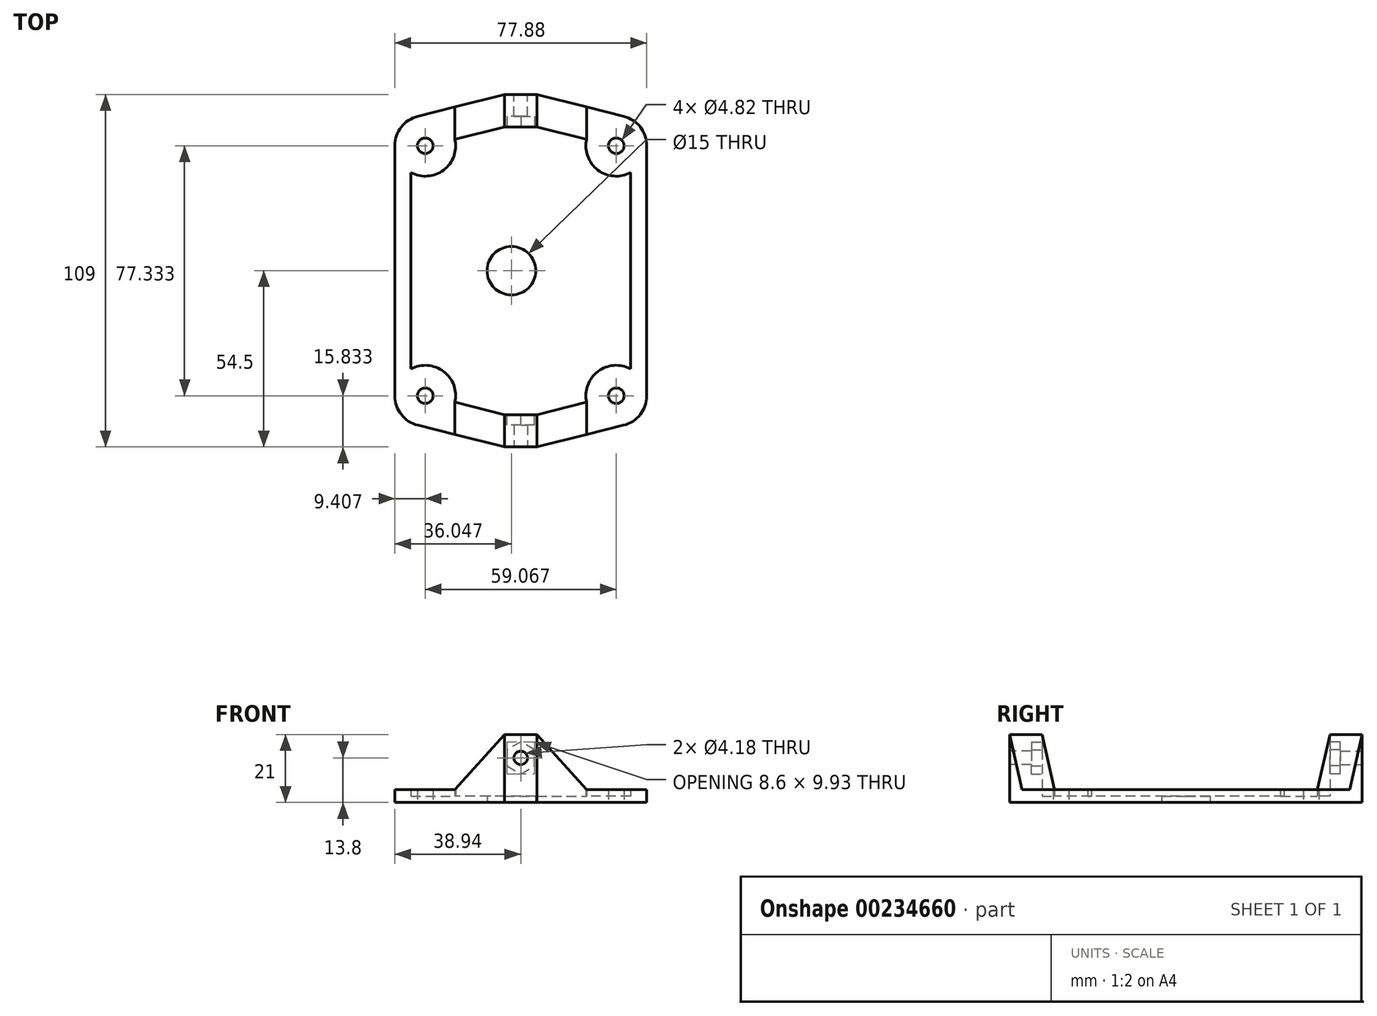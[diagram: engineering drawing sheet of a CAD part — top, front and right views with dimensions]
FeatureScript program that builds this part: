
annotation { "Feature Type Name" : "Feature", "Feature Type Description" : "" }
export const myFeature = defineFeature(function(context is Context, id is Id, definition is map)
    precondition{}
    {
        {
            var Q0;
            Q0=qCreatedBy(makeId("Top.planeOp"),FACE);
            var sketch = newSketch(context, id + "F0", { "sketchPlane" : qUnion([Q0])});
            skLineSegment(sketch, "E0.top", {"start": v(44.3, 58) * mm, "end": v(-44.3, 58) * mm, "construction": true});
            skLineSegment(sketch, "E0.left", {"start": v(44.3, -58) * mm, "end": v(44.3, 58) * mm, "construction": true});
            skLineSegment(sketch, "E0.right", {"start": v(-44.3, -58) * mm, "end": v(-44.3, 58) * mm, "construction": true});
            skPoint(sketch, "E0.middle", {"position": v(0, 0) * mm});
            skLineSegment(sketch, "E1.0", {"start": v(45.3, 59) * mm, "end": v(-45.3, 59) * mm, "construction": true});
            skLineSegment(sketch, "E1.1", {"start": v(45.3, -59) * mm, "end": v(45.3, 59) * mm, "construction": true});
            skLineSegment(sketch, "E1.2", {"start": v(45.3, -59) * mm, "end": v(-45.3, -59) * mm, "construction": true});
            skLineSegment(sketch, "E1.3", {"start": v(-45.3, -59) * mm, "end": v(-45.3, 59) * mm, "construction": true});
            skLineSegment(sketch, "E2", {"start": v(-5, -58) * mm, "end": v(-5, -54.5) * mm, "construction": true});
            skLineSegment(sketch, "E3", {"start": v(-5, -54.5) * mm, "end": v(5, -54.5) * mm, "construction": true});
            skLineSegment(sketch, "E4", {"start": v(5, -54.5) * mm, "end": v(5, -58) * mm, "construction": true});
            skPoint(sketch, "E5", {"position": v(0, 58) * mm});
            skLineSegment(sketch, "E6", {"start": v(-44.3, -38.67) * mm, "end": v(-29.53, -38.67) * mm, "construction": true});
            skLineSegment(sketch, "E7", {"start": v(-29.53, -38.67) * mm, "end": v(-14.77, -38.67) * mm, "construction": true});
            skLineSegment(sketch, "E8", {"start": v(-14.77, -38.67) * mm, "end": v(0, -38.67) * mm, "construction": true});
            skLineSegment(sketch, "E9", {"start": v(0, -38.67) * mm, "end": v(14.77, -38.67) * mm, "construction": true});
            skLineSegment(sketch, "E10", {"start": v(14.77, -38.67) * mm, "end": v(29.53, -38.67) * mm, "construction": true});
            skLineSegment(sketch, "E11", {"start": v(29.53, -38.67) * mm, "end": v(44.3, -38.67) * mm, "construction": true});
            skLineSegment(sketch, "E12", {"start": v(-29.53, -58) * mm, "end": v(-29.53, -38.67) * mm, "construction": true});
            skLineSegment(sketch, "E13", {"start": v(-29.53, 19.33) * mm, "end": v(-29.53, 38.67) * mm, "construction": true});
            skLineSegment(sketch, "E14", {"start": v(-29.53, 38.67) * mm, "end": v(-29.53, 58) * mm, "construction": true});
            skLineSegment(sketch, "E15", {"start": v(-29.53, -19.33) * mm, "end": v(-29.53, -38.67) * mm, "construction": true});
            skLineSegment(sketch, "E16", {"start": v(-29.53, 38.67) * mm, "end": v(-14.77, 38.67) * mm, "construction": true});
            skLineSegment(sketch, "E17", {"start": v(-14.77, 38.67) * mm, "end": v(0, 38.67) * mm, "construction": true});
            skLineSegment(sketch, "E18", {"start": v(0, 38.67) * mm, "end": v(14.77, 38.67) * mm, "construction": true});
            skLineSegment(sketch, "E19", {"start": v(14.77, 38.67) * mm, "end": v(29.53, 38.67) * mm, "construction": true});
            skLineSegment(sketch, "E20", {"start": v(29.53, 38.67) * mm, "end": v(44.3, 38.67) * mm, "construction": true});
            skLineSegment(sketch, "E21", {"start": v(-29.53, 38.67) * mm, "end": v(-44.3, 38.67) * mm, "construction": true});
            skLineSegment(sketch, "E22", {"start": v(29.53, 58) * mm, "end": v(29.53, 38.67) * mm, "construction": true});
            skLineSegment(sketch, "E23", {"start": v(29.53, 19.33) * mm, "end": v(29.53, 0) * mm, "construction": true});
            skLineSegment(sketch, "E24", {"start": v(29.53, 0) * mm, "end": v(29.53, -19.33) * mm, "construction": true});
            skLineSegment(sketch, "E25", {"start": v(29.53, -19.33) * mm, "end": v(29.53, -38.67) * mm, "construction": true});
            skLineSegment(sketch, "E26", {"start": v(29.53, -58) * mm, "end": v(29.53, -38.67) * mm, "construction": true});
            skLineSegment(sketch, "E27", {"start": v(29.53, 38.67) * mm, "end": v(29.53, 19.33) * mm, "construction": true});
            skLineSegment(sketch, "E28", {"start": v(-29.53, -19.33) * mm, "end": v(-29.53, 0) * mm, "construction": true});
            skLineSegment(sketch, "E29", {"start": v(-29.53, 0) * mm, "end": v(-29.53, 19.33) * mm, "construction": true});
            skCircle(sketch, "E30", {"center": v(-29.53, -38.67) * mm, "radius": 2.41 * mm});
            skCircle(sketch, "E31", {"center": v(-29.53, 38.67) * mm, "radius": 2.41 * mm});
            skCircle(sketch, "E32", {"center": v(29.53, 38.67) * mm, "radius": 2.41 * mm});
            skCircle(sketch, "E33", {"center": v(29.53, -38.67) * mm, "radius": 2.41 * mm});
            skLineSegment(sketch, "E34", {"start": v(-5, -54.5) * mm, "end": v(-2.31, -54.5) * mm});
            skCircle(sketch, "E35.0", {"center": v(29.53, -38.67) * mm, "radius": 9.4 * mm});
            skCircle(sketch, "E36.0", {"center": v(-29.53, 38.67) * mm, "radius": 9.41 * mm});
            skCircle(sketch, "E37.0", {"center": v(29.53, 38.67) * mm, "radius": 9.41 * mm});
            skCircle(sketch, "E38.0", {"center": v(-29.53, -38.67) * mm, "radius": 9.4 * mm});
            skLineSegment(sketch, "E39", {"start": v(38.94, -38.67) * mm, "end": v(38.94, 38.67) * mm});
            skLineSegment(sketch, "E40", {"start": v(-38.94, -38.67) * mm, "end": v(-38.94, 38.67) * mm});
            skLineSegment(sketch, "E41", {"start": v(29.53, -58) * mm, "end": v(44.3, -58) * mm, "construction": true});
            skLineSegment(sketch, "E42", {"start": v(-44.3, -58) * mm, "end": v(-29.53, -58) * mm, "construction": true});
            skLineSegment(sketch, "E43", {"start": v(-5, -58) * mm, "end": v(-29.53, -58) * mm, "construction": true});
            skLineSegment(sketch, "E44", {"start": v(-5, -58) * mm, "end": v(5, -58) * mm, "construction": true});
            skLineSegment(sketch, "E45", {"start": v(5, -58) * mm, "end": v(29.53, -58) * mm, "construction": true});
            skLineSegment(sketch, "E46", {"start": v(-5, -54.5) * mm, "end": v(-31.82, -47.8) * mm});
            skLineSegment(sketch, "E47", {"start": v(5, -54.5) * mm, "end": v(31.82, -47.8) * mm});
            skLineSegment(sketch, "E48", {"start": v(-2.31, -54.5) * mm, "end": v(-2.31, -59) * mm, "construction": true});
            skLineSegment(sketch, "E49", {"start": v(2.31, -54.5) * mm, "end": v(2.31, -59) * mm, "construction": true});
            skLineSegment(sketch, "E50", {"start": v(-2.31, -54.5) * mm, "end": v(2.31, -54.5) * mm});
            skLineSegment(sketch, "E51", {"start": v(2.31, -54.5) * mm, "end": v(5, -54.5) * mm});
            skLineSegment(sketch, "E52.MirrorCS", {"start": v(-5, 58) * mm, "end": v(-5, 54.5) * mm, "construction": true});
            skLineSegment(sketch, "E53.MirrorCS", {"start": v(-5, 54.5) * mm, "end": v(5, 54.5) * mm});
            skLineSegment(sketch, "E54.MirrorCS", {"start": v(5, 54.5) * mm, "end": v(5, 58) * mm, "construction": true});
            skLineSegment(sketch, "E55.MirrorCS", {"start": v(2.31, 54.5) * mm, "end": v(2.31, 59) * mm, "construction": true});
            skLineSegment(sketch, "E56.MirrorCS", {"start": v(-2.31, 54.5) * mm, "end": v(-2.31, 59) * mm, "construction": true});
            skLineSegment(sketch, "E57", {"start": v(-5, 54.5) * mm, "end": v(-31.82, 47.8) * mm});
            skLineSegment(sketch, "E58", {"start": v(5, 54.5) * mm, "end": v(31.82, 47.8) * mm});
            skLineSegment(sketch, "E59", {"start": v(5, 44.5) * mm, "end": v(20.34, 40.67) * mm});
            skLineSegment(sketch, "E60", {"start": v(-5, 44.5) * mm, "end": v(-20.34, 40.67) * mm});
            skLineSegment(sketch, "E61", {"start": v(-5, 54.5) * mm, "end": v(-5, 44.5) * mm});
            skLineSegment(sketch, "E62", {"start": v(5, 54.5) * mm, "end": v(5, 44.5) * mm});
            skLineSegment(sketch, "E63", {"start": v(-5, 44.5) * mm, "end": v(5, 44.5) * mm});
            skLineSegment(sketch, "E64.MirrorCS", {"start": v(-5, -44.5) * mm, "end": v(-20.34, -40.67) * mm});
            skLineSegment(sketch, "E65.MirrorCS", {"start": v(-5, -54.5) * mm, "end": v(-5, -44.5) * mm});
            skLineSegment(sketch, "E66.MirrorCS", {"start": v(-5, -44.5) * mm, "end": v(5, -44.5) * mm});
            skLineSegment(sketch, "E67.MirrorCS", {"start": v(5, -54.5) * mm, "end": v(5, -44.5) * mm});
            skLineSegment(sketch, "E68.MirrorCS", {"start": v(5, -44.5) * mm, "end": v(20.34, -40.67) * mm});
            skLineSegment(sketch, "E69", {"start": v(-33.94, 30.35) * mm, "end": v(-33.94, -30.35) * mm});
            skLineSegment(sketch, "E70.MirrorCS", {"start": v(33.94, 30.35) * mm, "end": v(33.94, -30.35) * mm});
            skCircle(sketch, "E71", {"center": v(-2.9, 0) * mm, "radius": 7.5 * mm});
            skLineSegment(sketch, "E72", {"start": v(-2.09, -54.5) * mm, "end": v(-2.1, -44.5) * mm, "construction": true});
            skLineSegment(sketch, "E73", {"start": v(2.09, -54.5) * mm, "end": v(2.1, -44.5) * mm, "construction": true});
            skLineSegment(sketch, "E74.MirrorCS", {"start": v(-2.1, 54.5) * mm, "end": v(-2.1, 44.5) * mm, "construction": true});
            skLineSegment(sketch, "E75.MirrorCS", {"start": v(2.1, 54.5) * mm, "end": v(2.1, 44.5) * mm, "construction": true});
            skSolve(sketch);
        }
        {
            var Q0;
            {var subQ2=sQuery(id+"F0.wireOp",EDGE,"E59");Q0=makeQuery(id+"F0.imprint","IMPRINT",FACE,{"disambiguationData":[TD([[makeQuery(id+"F0.imprint","IMPRINT",EDGE,{"derivedFrom":subQ2}),-1.0]])]});}
            extrude(context, id + "F1", {"entities" : qUnion([Q0]), "depth" : 2 * mm});
        }
        {
            var Q0;
            Q0=makeQuery(id+"F0.imprint","IMPRINT",FACE,{"disambiguationData":[TD([[makeQuery(id+"F0.imprint","IMPRINT",EDGE,{"derivedFrom":sQuery(id+"F0.wireOp",EDGE,"E30")}),-1.0]])]});
            var Q1;
            Q1=makeQuery(id+"F0.imprint","IMPRINT",FACE,{"disambiguationData":[TD([[makeQuery(id+"F0.imprint","IMPRINT",EDGE,{"derivedFrom":sQuery(id+"F0.wireOp",EDGE,"E31")}),-1.0]])]});
            var Q2;
            Q2=makeQuery(id+"F0.imprint","IMPRINT",FACE,{"disambiguationData":[TD([[makeQuery(id+"F0.imprint","IMPRINT",EDGE,{"derivedFrom":sQuery(id+"F0.wireOp",EDGE,"E32")}),-1.0]])]});
            var Q3;
            Q3=makeQuery(id+"F0.imprint","IMPRINT",FACE,{"disambiguationData":[TD([[makeQuery(id+"F0.imprint","IMPRINT",EDGE,{"derivedFrom":sQuery(id+"F0.wireOp",EDGE,"E33")}),-1.0]])]});
            var Q4;
            {var subQ0=sQuery(id+"F0.wireOp",EDGE,"E39");Q4=makeQuery(id+"F0.imprint","IMPRINT",FACE,{"disambiguationData":[TD([[makeQuery(id+"F0.imprint","IMPRINT",EDGE,{"derivedFrom":subQ0}),1.0]])]});}
            var Q5;
            {var subQ0=sQuery(id+"F0.wireOp",EDGE,"E40");Q5=makeQuery(id+"F0.imprint","IMPRINT",FACE,{"disambiguationData":[TD([[makeQuery(id+"F0.imprint","IMPRINT",EDGE,{"derivedFrom":subQ0}),-1.0]])]});}
            extrude(context, id + "F2", {"entities" : qUnion([Q0, Q1, Q2, Q3, Q4, Q5]), "operationType" : NewBodyOperationType.ADD, "depth" : 4 * mm});
        }
        {
            var Q0;
            {var subQ0=sQuery(id+"F0.wireOp",EDGE,"E47");Q0=makeQuery(id+"F0.imprint","IMPRINT",FACE,{"disambiguationData":[TD([[makeQuery(id+"F0.imprint","IMPRINT",EDGE,{"derivedFrom":subQ0}),1.0]])]});}
            extrude(context, id + "F3", {"entities" : qUnion([Q0]), "operationType" : NewBodyOperationType.ADD, "depth" : 21 * mm});
        }
        {
            var Q0;
            Q0=makeQuery(id+"F3.opExtrude","SWEPT_FACE",FACE,{"disambiguationData":[OSD([sQuery(id+"F0.wireOp",EDGE,"E68.MirrorCS")])]});
            var sketch = newSketch(context, id + "F4", { "sketchPlane" : qUnion([Q0])});
            skLineSegment(sketch, "E76", {"start": v(-9.87, 4) * mm, "end": v(5.94, 21) * mm});
            skSolve(sketch);
        }
        {
            var Q0;
            Q0=makeQuery(id+"F4.imprint","IMPRINT",FACE,{"disambiguationData":[TD([[makeQuery(id+"F4.imprint","IMPRINT",EDGE,{"derivedFrom":sQuery(id+"F4.wireOp",EDGE,"E76")}),1.0]])]});
            var Q1;
            Q1=makeQuery(id+"F3.opExtrude","CAP_EDGE",EDGE,{"disambiguationData":[OSD([sQuery(id+"F0.wireOp",EDGE,"E67.MirrorCS")])],"isStart":false});
            sweep(context, id + "F5", {"operationType" : NewBodyOperationType.REMOVE, "profiles" : qUnion([Q0]), "path" : qUnion([Q1])});
        }
        {
            var Q0;
            Q0=makeQuery(id+"F5.boolean.opBoolean","COPY",FACE,{"derivedFrom":makeQuery(id+"F5.opSweep","SWEPT_FACE",FACE,{"disambiguationData":[OSD([sQuery(id+"F0.wireOp",EDGE,"E35.0"),sQuery(id+"F0.wireOp",EDGE,"E67.MirrorCS"),sQuery(id+"F0.wireOp",EDGE,"E68.MirrorCS")])]})});
            extrude(context, id + "F6", {"entities" : qUnion([Q0]), "operationType" : NewBodyOperationType.REMOVE, "endBound" : BoundingType.UP_TO_NEXT, "oppositeDirection" : true, "depth" : 25 * mm});
        }
        {
            var Q0;
            {var subQ0=sQuery(id+"F0.wireOp",EDGE,"E46");Q0=makeQuery(id+"F0.imprint","IMPRINT",FACE,{"disambiguationData":[TD([[makeQuery(id+"F0.imprint","IMPRINT",EDGE,{"derivedFrom":subQ0}),-1.0]])]});}
            extrude(context, id + "F7", {"entities" : qUnion([Q0]), "operationType" : NewBodyOperationType.ADD, "depth" : 21 * mm});
        }
        {
            var Q0;
            Q0=makeQuery(id+"F7.opExtrude","SWEPT_FACE",FACE,{"disambiguationData":[OSD([sQuery(id+"F0.wireOp",EDGE,"E64.MirrorCS")])]});
            var sketch = newSketch(context, id + "F8", { "sketchPlane" : qUnion([Q0])});
            skLineSegment(sketch, "E77", {"start": v(-5.94, 21) * mm, "end": v(9.87, 4) * mm});
            skSolve(sketch);
        }
        {
            var Q0;
            Q0=makeQuery(id+"F8.imprint","IMPRINT",FACE,{"disambiguationData":[TD([[makeQuery(id+"F8.imprint","IMPRINT",EDGE,{"derivedFrom":sQuery(id+"F8.wireOp",EDGE,"E77")}),1.0]])]});
            var Q1;
            Q1=makeQuery(id+"F7.opExtrude","CAP_EDGE",EDGE,{"disambiguationData":[OSD([sQuery(id+"F0.wireOp",EDGE,"E65.MirrorCS")])],"isStart":false});
            sweep(context, id + "F9", {"operationType" : NewBodyOperationType.REMOVE, "profiles" : qUnion([Q0]), "path" : qUnion([Q1])});
        }
        {
            var Q0;
            Q0=makeQuery(id+"F9.boolean.opBoolean","COPY",FACE,{"derivedFrom":makeQuery(id+"F9.opSweep","SWEPT_FACE",FACE,{"disambiguationData":[OSD([sQuery(id+"F0.wireOp",EDGE,"E38.0"),sQuery(id+"F0.wireOp",EDGE,"E64.MirrorCS"),sQuery(id+"F0.wireOp",EDGE,"E65.MirrorCS")])]})});
            extrude(context, id + "F10", {"entities" : qUnion([Q0]), "operationType" : NewBodyOperationType.REMOVE, "endBound" : BoundingType.UP_TO_NEXT, "oppositeDirection" : true, "depth" : 25 * mm});
        }
        {
            var Q0;
            {var subQ0=sQuery(id+"F0.wireOp",EDGE,"E58");Q0=makeQuery(id+"F0.imprint","IMPRINT",FACE,{"disambiguationData":[TD([[makeQuery(id+"F0.imprint","IMPRINT",EDGE,{"derivedFrom":subQ0}),-1.0]])]});}
            var Q1;
            {var subQ0=sQuery(id+"F0.wireOp",EDGE,"E57");Q1=makeQuery(id+"F0.imprint","IMPRINT",FACE,{"disambiguationData":[TD([[makeQuery(id+"F0.imprint","IMPRINT",EDGE,{"derivedFrom":subQ0}),1.0]])]});}
            extrude(context, id + "F11", {"entities" : qUnion([Q0, Q1]), "operationType" : NewBodyOperationType.ADD, "depth" : 21 * mm});
        }
        {
            var Q0;
            Q0=makeQuery(id+"F11.opExtrude","SWEPT_FACE",FACE,{"disambiguationData":[OSD([sQuery(id+"F0.wireOp",EDGE,"E60")])]});
            var sketch = newSketch(context, id + "F12", { "sketchPlane" : qUnion([Q0])});
            skLineSegment(sketch, "E78", {"start": v(5.94, 21) * mm, "end": v(-9.87, 4) * mm});
            skSolve(sketch);
        }
        {
            var Q0;
            Q0=makeQuery(id+"F11.opExtrude","SWEPT_FACE",FACE,{"disambiguationData":[OSD([sQuery(id+"F0.wireOp",EDGE,"E59")])]});
            var sketch = newSketch(context, id + "F13", { "sketchPlane" : qUnion([Q0])});
            skLineSegment(sketch, "E79", {"start": v(-5.94, 21) * mm, "end": v(9.87, 4) * mm});
            skSolve(sketch);
        }
        {
            var Q0;
            Q0=makeQuery(id+"F12.imprint","IMPRINT",FACE,{"disambiguationData":[TD([[makeQuery(id+"F12.imprint","IMPRINT",EDGE,{"derivedFrom":sQuery(id+"F12.wireOp",EDGE,"E78")}),-1.0]])]});
            var Q1;
            Q1=makeQuery(id+"F11.opExtrude","CAP_EDGE",EDGE,{"disambiguationData":[OSD([sQuery(id+"F0.wireOp",EDGE,"E61")])],"isStart":false});
            sweep(context, id + "F14", {"operationType" : NewBodyOperationType.REMOVE, "profiles" : qUnion([Q0]), "path" : qUnion([Q1])});
        }
        {
            var Q0;
            Q0=makeQuery(id+"F13.imprint","IMPRINT",FACE,{"disambiguationData":[TD([[makeQuery(id+"F13.imprint","IMPRINT",EDGE,{"derivedFrom":sQuery(id+"F13.wireOp",EDGE,"E79")}),1.0]])]});
            var Q1;
            Q1=makeQuery(id+"F11.opExtrude","CAP_EDGE",EDGE,{"disambiguationData":[OSD([sQuery(id+"F0.wireOp",EDGE,"E62")])],"isStart":false});
            sweep(context, id + "F15", {"operationType" : NewBodyOperationType.REMOVE, "profiles" : qUnion([Q0]), "path" : qUnion([Q1])});
        }
        {
            var Q0;
            Q0=makeQuery(id+"F15.boolean.opBoolean","COPY",FACE,{"derivedFrom":makeQuery(id+"F15.opSweep","SWEPT_FACE",FACE,{"disambiguationData":[OSD([sQuery(id+"F0.wireOp",EDGE,"E37.0"),sQuery(id+"F0.wireOp",EDGE,"E59"),sQuery(id+"F0.wireOp",EDGE,"E62")])]})});
            extrude(context, id + "F16", {"entities" : qUnion([Q0]), "operationType" : NewBodyOperationType.REMOVE, "endBound" : BoundingType.UP_TO_NEXT, "oppositeDirection" : true, "depth" : 25 * mm});
        }
        {
            var Q0;
            Q0=makeQuery(id+"F14.boolean.opBoolean","COPY",FACE,{"derivedFrom":makeQuery(id+"F14.opSweep","SWEPT_FACE",FACE,{"disambiguationData":[OSD([sQuery(id+"F0.wireOp",EDGE,"E36.0"),sQuery(id+"F0.wireOp",EDGE,"E60"),sQuery(id+"F0.wireOp",EDGE,"E61")])]})});
            extrude(context, id + "F17", {"entities" : qUnion([Q0]), "operationType" : NewBodyOperationType.REMOVE, "endBound" : BoundingType.UP_TO_NEXT, "oppositeDirection" : true, "depth" : 25 * mm});
        }
        {
            var Q0;
            {var subQ3=sQuery(id+"F0.wireOp",EDGE,"E61");Q0=makeQuery(id+"F0.imprint","IMPRINT",FACE,{"disambiguationData":[TD([[makeQuery(id+"F0.imprint","IMPRINT",EDGE,{"derivedFrom":subQ3}),1.0]])]});}
            var Q1;
            {var subQ3=sQuery(id+"F0.wireOp",EDGE,"E34");Q1=makeQuery(id+"F0.imprint","IMPRINT",FACE,{"disambiguationData":[TD([[makeQuery(id+"F0.imprint","IMPRINT",EDGE,{"derivedFrom":subQ3}),1.0]])]});}
            var Q2;
            {var subQ0=sQuery(id+"F0.wireOp",EDGE,"266f00a4-82cf-487b-820f-75a998bac8420.MirrorCS");Q2=makeQuery(id+"F0.imprint","IMPRINT",FACE,{"disambiguationData":[TD([[makeQuery(id+"F0.imprint","IMPRINT",EDGE,{"derivedFrom":subQ0}),-1.0]])]});}
            var Q3;
            {var subQ0=sQuery(id+"F0.wireOp",EDGE,"IAeXozkj-3vd1-ZeOr-YcZc-Ep6KovT17IZi");Q3=makeQuery(id+"F0.imprint","IMPRINT",FACE,{"disambiguationData":[TD([[makeQuery(id+"F0.imprint","IMPRINT",EDGE,{"derivedFrom":subQ0}),1.0]])]});}
            extrude(context, id + "F18", {"entities" : qUnion([Q0, Q1, Q2, Q3]), "operationType" : NewBodyOperationType.ADD, "depth" : 21 * mm});
        }
        {
            var Q0;
            Q0=makeQuery(id+"F18.opExtrude","SWEPT_FACE",FACE,{"disambiguationData":[OSD([sQuery(id+"F0.wireOp",EDGE,"E34"),sQuery(id+"F0.wireOp",EDGE,"E50"),sQuery(id+"F0.wireOp",EDGE,"E51")])]});
            var sketch = newSketch(context, id + "F19", { "sketchPlane" : qUnion([Q0])});
            skPoint(sketch, "E80.0", {"position": v(-2.09, 0) * mm});
            skPoint(sketch, "E81.0", {"position": v(2.1, 0) * mm});
            skPoint(sketch, "E82.0", {"position": v(0, 0) * mm});
            skCircle(sketch, "E83", {"center": v(0, 13.8) * mm, "radius": 2.1 * mm});
            skLineSegment(sketch, "E84", {"start": v(-2.09, 0) * mm, "end": v(-2.1, 21) * mm, "construction": true});
            skLineSegment(sketch, "E85", {"start": v(2.1, 0) * mm, "end": v(2.1, 21) * mm, "construction": true});
            skPoint(sketch, "E86.0", {"position": v(2.09, 0) * mm});
            skSolve(sketch);
        }
        {
            var Q0;
            Q0=makeQuery(id+"F18.opExtrude","SWEPT_FACE",FACE,{"disambiguationData":[OSD([sQuery(id+"F0.wireOp",EDGE,"E53.MirrorCS")])]});
            var sketch = newSketch(context, id + "F20", { "sketchPlane" : qUnion([Q0])});
            skLineSegment(sketch, "E87.0", {"start": v(2.09, 0) * mm, "end": v(2.09, 21) * mm, "construction": true});
            skLineSegment(sketch, "E88.0", {"start": v(-2.1, 0) * mm, "end": v(-2.1, 21) * mm, "construction": true});
            skCircle(sketch, "E89.0", {"center": v(0, 13.8) * mm, "radius": 2.1 * mm});
            skSolve(sketch);
        }
        {
            var Q0;
            Q0 = qSketchRegion(id + "F20", true);
            extrude(context, id + "F21", {"entities" : qUnion([Q0]), "operationType" : NewBodyOperationType.REMOVE, "endBound" : BoundingType.UP_TO_NEXT, "oppositeDirection" : true, "depth" : 3 * mm});
        }
        {
            var Q0;
            Q0=makeQuery(id+"F19.imprint","IMPRINT",FACE,{"disambiguationData":[TD([[makeQuery(id+"F19.imprint","IMPRINT",EDGE,{"derivedFrom":sQuery(id+"F19.wireOp",EDGE,"E83")}),1.0]])]});
            extrude(context, id + "F22", {"entities" : qUnion([Q0]), "operationType" : NewBodyOperationType.REMOVE, "endBound" : BoundingType.UP_TO_NEXT, "oppositeDirection" : true, "depth" : 3 * mm});
        }
        {
            var Q0;
            Q0=makeQuery(id+"F18.opExtrude","SWEPT_FACE",FACE,{"disambiguationData":[OSD([sQuery(id+"F0.wireOp",EDGE,"E66.MirrorCS")])]});
            var sketch = newSketch(context, id + "F23", { "sketchPlane" : qUnion([Q0])});
            skCircle(sketch, "E90.0", {"center": v(0, 13.8) * mm, "radius": 2.1 * mm});
            skCircle(sketch, "E91.cCircle", {"center": v(0, 13.8) * mm, "radius": 4.3 * mm, "construction": true});
            skLineSegment(sketch, "E91.0", {"start": v(4.3, 16.28) * mm, "end": v(4.3, 11.32) * mm});
            skLineSegment(sketch, "E91.1", {"start": v(4.3, 11.32) * mm, "end": v(0, 8.83) * mm});
            skLineSegment(sketch, "E91.2", {"start": v(0, 8.83) * mm, "end": v(-4.3, 11.32) * mm});
            skLineSegment(sketch, "E91.3", {"start": v(-4.3, 11.32) * mm, "end": v(-4.3, 16.28) * mm});
            skLineSegment(sketch, "E91.4", {"start": v(-4.3, 16.28) * mm, "end": v(0, 18.77) * mm});
            skLineSegment(sketch, "E91.5", {"start": v(0, 18.77) * mm, "end": v(4.3, 16.28) * mm});
            skPoint(sketch, "E91.0.midPoint", {"position": v(4.3, 13.8) * mm});
            skSolve(sketch);
        }
        {
            var Q0;
            Q0=makeQuery(id+"F18.opExtrude","SWEPT_FACE",FACE,{"disambiguationData":[OSD([sQuery(id+"F0.wireOp",EDGE,"E63")])]});
            var sketch = newSketch(context, id + "F24", { "sketchPlane" : qUnion([Q0])});
            skLineSegment(sketch, "E92.0", {"start": v(4.3, 11.32) * mm, "end": v(4.3, 16.28) * mm});
            skPoint(sketch, "E93.0", {"position": v(4.3, 16.28) * mm});
            skLineSegment(sketch, "E94.0", {"start": v(4.3, 16.28) * mm, "end": v(0, 18.77) * mm});
            skPoint(sketch, "E95.0", {"position": v(0, 18.77) * mm});
            skLineSegment(sketch, "E96.0", {"start": v(0, 18.77) * mm, "end": v(-4.3, 16.28) * mm});
            skLineSegment(sketch, "E97.0", {"start": v(-4.3, 16.28) * mm, "end": v(-4.3, 11.32) * mm});
            skPoint(sketch, "E98.0", {"position": v(-4.3, 11.32) * mm});
            skLineSegment(sketch, "E99.0", {"start": v(-4.3, 11.32) * mm, "end": v(0, 8.83) * mm});
            skLineSegment(sketch, "E100.0", {"start": v(0, 8.83) * mm, "end": v(4.3, 11.32) * mm});
            skPoint(sketch, "E101.0", {"position": v(0, 8.83) * mm});
            skPoint(sketch, "E102.0", {"position": v(-4.3, 16.28) * mm});
            skPoint(sketch, "E103.0", {"position": v(4.3, 11.32) * mm});
            skSolve(sketch);
        }
        {
            var Q0;
            Q0=makeQuery(id+"F24.imprint","IMPRINT",FACE,{"disambiguationData":[TD([[makeQuery(id+"F24.imprint","IMPRINT",EDGE,{"derivedFrom":sQuery(id+"F24.wireOp",EDGE,"E92.0")}),1.0]])]});
            extrude(context, id + "F25", {"entities" : qUnion([Q0]), "operationType" : NewBodyOperationType.REMOVE, "oppositeDirection" : true, "depth" : 3.3 * mm});
        }
        {
            var Q0;
            Q0=makeQuery(id+"F23.imprint","IMPRINT",FACE,{"disambiguationData":[TD([[makeQuery(id+"F23.imprint","IMPRINT",EDGE,{"derivedFrom":sQuery(id+"F23.wireOp",EDGE,"E90.0")}),1.0]])]});
            extrude(context, id + "F26", {"entities" : qUnion([Q0]), "operationType" : NewBodyOperationType.REMOVE, "oppositeDirection" : true, "depth" : 3.3 * mm});
        }
    });
